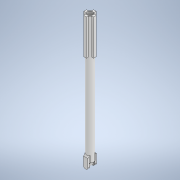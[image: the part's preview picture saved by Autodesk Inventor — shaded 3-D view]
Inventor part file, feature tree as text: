
AUTODESK INVENTOR PART (.ipt)
format: ipt  version: 2022 (Build 260153000, 153)  size: 257,536 bytes
history: native  units: in
note: dims shown in document units (in); Inventor stores cm internally (conversion verified against a paired STEP export)
features: extrude x5, fillet x5, sketch x5
ambient origin geometry x8: Origin, YZ Plane, XZ Plane, XY Plane, X Axis, Y Axis, Z Axis, Center Point
bodies: Body1 (feature_tree)
feature tree (15):
  extrude  "Extrusion7"  Depth=4.6063in TaperAngle=0.0deg
  extrude  "Extrusion8"  Depth=0.1142in
  extrude  "Extrusion9"  Depth=0.1142in
  fillet  "Fillet1"  Radius=0.1142in
  fillet  "Fillet3"  Radius=0.1142in
  fillet  "Fillet5"  Radius=0.1142in
  fillet  "Fillet6"  Radius=0.1142in
  fillet  "Fillet7"  Radius=0.7087in
  extrude  "Extrusion11"  Depth=0.189in
  extrude  "Extrusion12"  Depth=0.0945in
  sketch  "Sketch7"  dims[d71=0.2953in d72=4.6063in d73=0.0in]
  sketch  "Sketch8"  dims[d74=0.1142in d75=0.1142in]
  sketch  "Sketch9"  dims[d76=0.1142in d77=0.1142in d78=0.1142in d79=0.1142in d80=0.1142in d81=0.1142in d82=0.7087in d83=0.0in]
  sketch  "Sketch11"  dims[d84=0.7874in d85=0.0in d86=0.189in]
  sketch  "Sketch12"  dims[d87=0.0728in d88=0.1083in d90=0.0728in d91=0.2165in d93=0.2362in d94=0.1969in d95=0.0in d96=0.0in d97=0.0787in d99=0.0394in d106=0.0394in d107=0.0197in d108=0.0945in d109=0.1181in d110=0.0984in d111=0.0984in d112=0.3937in d113=0.0in d115=0.2362in d116=0.315in d117=0.0in d121=0.0945in d122=0.0945in d123=0.189in d98=0.0in d100=0.0in d101=0.0in d118=0.0197in d119=0.0344in d120=0.0197in]
